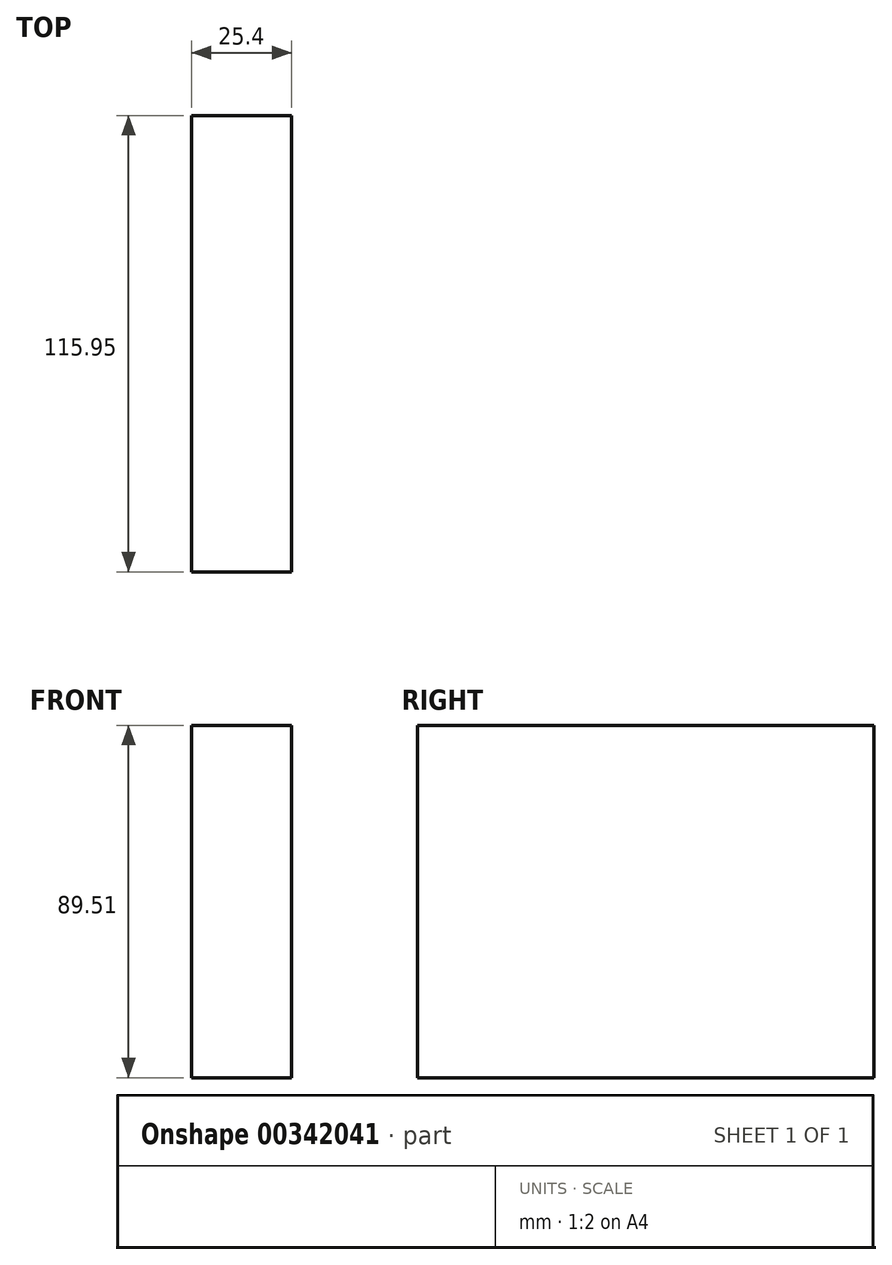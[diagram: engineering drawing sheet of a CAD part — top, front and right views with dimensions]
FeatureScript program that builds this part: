
annotation { "Feature Type Name" : "Feature", "Feature Type Description" : "" }
export const myFeature = defineFeature(function(context is Context, id is Id, definition is map)
    precondition{}
    {
        {
            var Q0;
            Q0=qCreatedBy(makeId("Right.planeOp"),FACE);
            var sketch = newSketch(context, id + "F0", { "sketchPlane" : qUnion([Q0])});
            skLineSegment(sketch, "E0.bottom", {"start": v(97.64, -38.43) * mm, "end": v(-18.31, -38.43) * mm});
            skLineSegment(sketch, "E0.top", {"start": v(97.64, 51.08) * mm, "end": v(-18.31, 51.08) * mm});
            skLineSegment(sketch, "E0.left", {"start": v(97.64, -38.43) * mm, "end": v(97.64, 51.08) * mm});
            skLineSegment(sketch, "E0.right", {"start": v(-18.31, -38.43) * mm, "end": v(-18.31, 51.08) * mm});
            skSolve(sketch);
        }
        {
            var Q0;
            Q0=makeQuery(id+"F0.imprint","IMPRINT",FACE,{"disambiguationData":[TD([[makeQuery(id+"F0.imprint","IMPRINT",EDGE,{"derivedFrom":sQuery(id+"F0.wireOp",EDGE,"E0.bottom")}),-1.0]])]});
            extrude(context, id + "F1", {"entities" : qUnion([Q0]), "depth" : 25.4 * mm});
        }
    });
